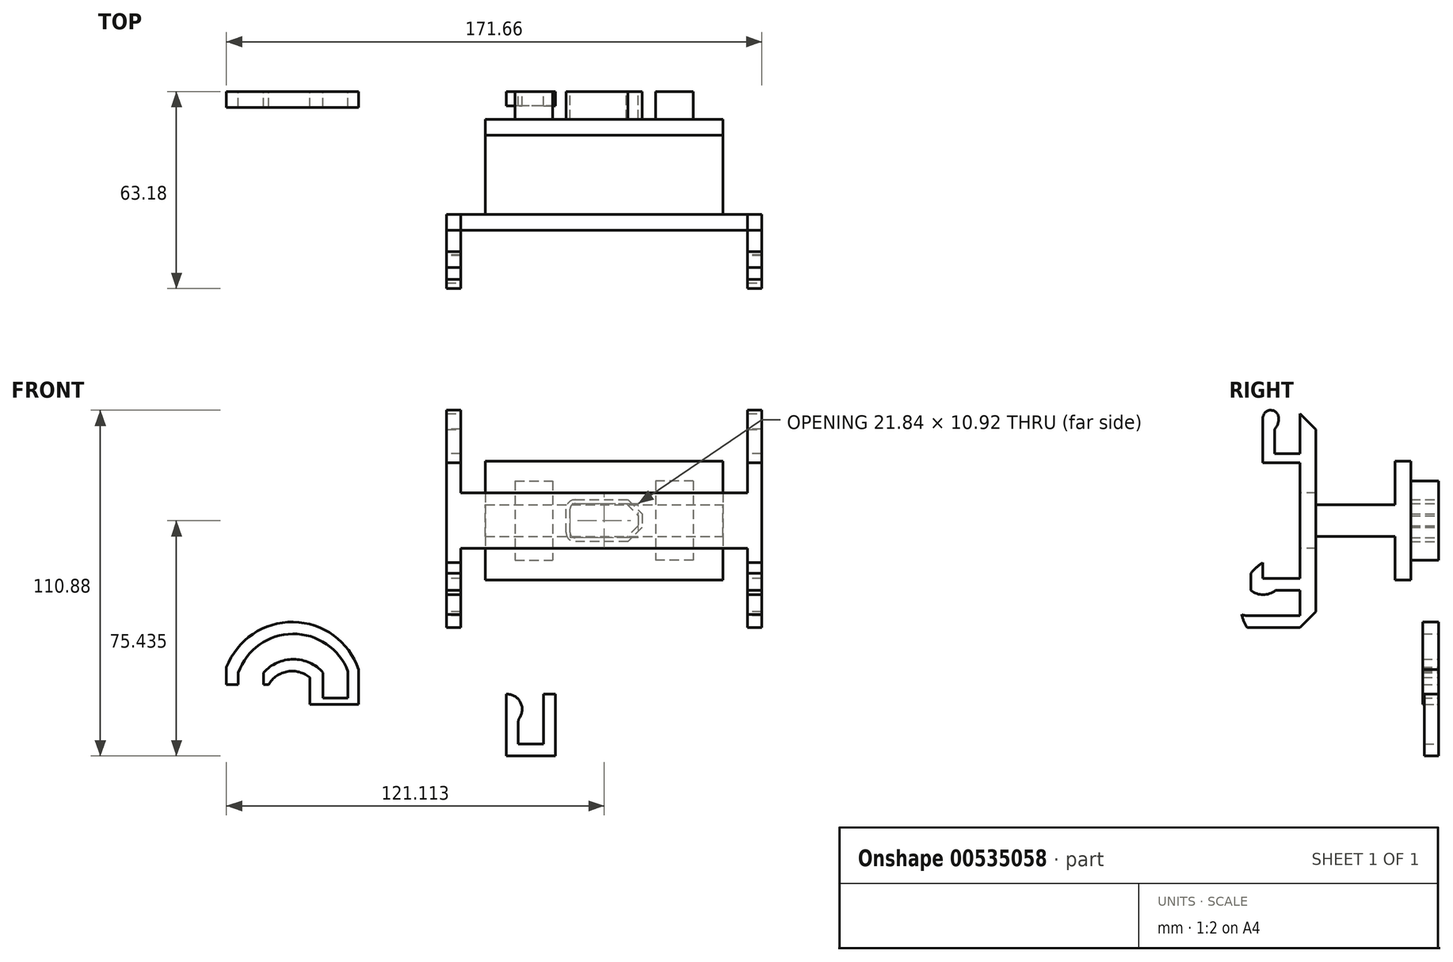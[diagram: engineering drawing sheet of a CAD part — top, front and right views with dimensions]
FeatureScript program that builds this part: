
annotation { "Feature Type Name" : "Feature", "Feature Type Description" : "" }
export const myFeature = defineFeature(function(context is Context, id is Id, definition is map)
    precondition{}
    {
        {
            var Q0;
            Q0=qCreatedBy(makeId("Front.planeOp"),FACE);
            var sketch = newSketch(context, id + "F0", { "sketchPlane" : qUnion([Q0])});
            skArc(sketch, "E0", {"start": v(-13.67, 11.5) * mm, "mid": v(-23.2, 15.8) * mm, "end": v(-32.72, 11.5) * mm});
            skArc(sketch, "E1", {"start": v(-5.68, 11.86) * mm, "mid": v(-23.39, 23.92) * mm, "end": v(-40.85, 11.5) * mm});
            skLineSegment(sketch, "E2", {"start": v(-13.67, 11.5) * mm, "end": v(-13.67, 3.37) * mm});
            skLineSegment(sketch, "E3", {"start": v(-13.67, 3.37) * mm, "end": v(-5.68, 3.37) * mm});
            skLineSegment(sketch, "E4", {"start": v(-5.68, 3.37) * mm, "end": v(-5.68, 11.86) * mm});
            skArc(sketch, "E5.0", {"start": v(-17.86, 9.9) * mm, "mid": v(-25.04, 11.87) * mm, "end": v(-31.2, 7.69) * mm});
            skArc(sketch, "E5.1", {"start": v(-2.25, 12.53) * mm, "mid": v(-23.21, 27.73) * mm, "end": v(-44.66, 13.21) * mm});
            skLineSegment(sketch, "E5.2", {"start": v(-2.25, 1.34) * mm, "end": v(-2.25, 12.53) * mm});
            skLineSegment(sketch, "E5.3", {"start": v(-31.2, 7.69) * mm, "end": v(-32.72, 7.69) * mm});
            skLineSegment(sketch, "E5.4", {"start": v(-17.86, 1.34) * mm, "end": v(-2.25, 1.34) * mm});
            skLineSegment(sketch, "E5.5", {"start": v(-17.86, 9.9) * mm, "end": v(-17.86, 1.34) * mm});
            skLineSegment(sketch, "E6", {"start": v(-32.72, 11.5) * mm, "end": v(-32.72, 7.69) * mm});
            skLineSegment(sketch, "E7", {"start": v(-40.85, 11.5) * mm, "end": v(-40.85, 7.69) * mm});
            skLineSegment(sketch, "E8.trimOffspring", {"start": v(-40.85, 7.69) * mm, "end": v(-44.66, 7.69) * mm});
            skLineSegment(sketch, "E9", {"start": v(-44.66, 7.69) * mm, "end": v(-44.66, 13.21) * mm});
            skSolve(sketch);
        }
        {
            var Q0;
            Q0 = qSketchRegion(id + "F0", true);
            extrude(context, id + "F1", {"entities" : qUnion([Q0]), "depth" : 5.08 * mm, "offsetDistance" : 25.4 * mm});
        }
        {
            var Q0;
            Q0=qCreatedBy(makeId("Front.planeOp"),FACE);
            var sketch = newSketch(context, id + "F2", { "sketchPlane" : qUnion([Q0])});
            skLineSegment(sketch, "E10", {"start": v(60.82, 4.57) * mm, "end": v(60.82, -11.43) * mm});
            skLineSegment(sketch, "E11", {"start": v(60.82, -11.43) * mm, "end": v(57.01, -11.43) * mm});
            skLineSegment(sketch, "E12", {"start": v(57.01, -11.43) * mm, "end": v(48.88, -11.43) * mm});
            skLineSegment(sketch, "E13", {"start": v(48.88, -11.43) * mm, "end": v(48.88, -3.56) * mm});
            skLineSegment(sketch, "E14", {"start": v(48.88, -11.43) * mm, "end": v(45.07, -11.43) * mm});
            skLineSegment(sketch, "E15", {"start": v(57.01, -11.43) * mm, "end": v(57.01, 4.57) * mm});
            skLineSegment(sketch, "E16", {"start": v(48.88, -11.43) * mm, "end": v(48.88, -15.24) * mm});
            skLineSegment(sketch, "E17", {"start": v(60.82, -11.43) * mm, "end": v(60.82, -15.24) * mm});
            skLineSegment(sketch, "E18", {"start": v(60.82, -15.24) * mm, "end": v(45.07, -15.24) * mm});
            skPoint(sketch, "E19.endSnap0", {"position": v(45.58, 10.16) * mm});
            skLineSegment(sketch, "E20", {"start": v(48.88, 0) * mm, "end": v(50.15, 0) * mm});
            skLineSegment(sketch, "E21", {"start": v(45.07, -15.24) * mm, "end": v(45.07, 4.57) * mm});
            skLineSegment(sketch, "E22", {"start": v(57.01, 4.57) * mm, "end": v(60.82, 4.57) * mm});
            skArc(sketch, "E23", {"start": v(48.88, -3.56) * mm, "mid": v(49.7, 1.78) * mm, "end": v(45.07, 4.57) * mm});
            skSolve(sketch);
        }
        {
            var Q0;
            Q0=makeQuery(id+"F2.imprint","IMPRINT",FACE,{"disambiguationData":[TD([[makeQuery(id+"F2.imprint","IMPRINT",EDGE,{"derivedFrom":sQuery(id+"F2.wireOp",EDGE,"RD1xtZW0-n7MP-K1y6-x4sb-vJHUDeZWFKJs")}),1.0]])]});
            var Q1;
            {var subQ0=sQuery(id+"F2.wireOp",EDGE,"E14");Q1=makeQuery(id+"F2.imprint","IMPRINT",FACE,{"disambiguationData":[TD([[makeQuery(id+"F2.imprint","IMPRINT",EDGE,{"derivedFrom":subQ0}),1.0]])]});}
            var Q2;
            {var subQ3=sQuery(id+"F2.wireOp",EDGE,"tBU92qzq-POFk-Bsx7-1rhX-yegVpMIyp9l8");Q2=makeQuery(id+"F2.imprint","IMPRINT",FACE,{"disambiguationData":[TD([[makeQuery(id+"F2.imprint","IMPRINT",EDGE,{"derivedFrom":subQ3}),1.0]])]});}
            var Q3;
            Q3=makeQuery(id+"F2.imprint","IMPRINT",FACE,{"disambiguationData":[TD([[makeQuery(id+"F2.imprint","IMPRINT",EDGE,{"derivedFrom":sQuery(id+"F2.wireOp",EDGE,"E11")}),1.0]])]});
            var Q4;
            Q4=makeQuery(id+"F2.imprint","IMPRINT",FACE,{"disambiguationData":[TD([[makeQuery(id+"F2.imprint","IMPRINT",EDGE,{"derivedFrom":sQuery(id+"F2.wireOp",EDGE,"E13")}),1.0]])]});
            var Q5;
            {var subQ4=sQuery(id+"F2.wireOp",EDGE,"hMDouHN4-NCv2-R56o-Xmj0-efINNTKzQc0g");Q5=makeQuery(id+"F2.imprint","IMPRINT",FACE,{"disambiguationData":[TD([[makeQuery(id+"F2.imprint","IMPRINT",EDGE,{"derivedFrom":subQ4}),1.0]])]});}
            var Q6;
            {var subQ0=sQuery(id+"F2.wireOp",EDGE,"O27wem4o-anWz-oDyt-zTwi-oJhownXQFu4R");Q6=makeQuery(id+"F2.imprint","IMPRINT",FACE,{"disambiguationData":[TD([[makeQuery(id+"F2.imprint","IMPRINT",EDGE,{"derivedFrom":subQ0}),1.0]])]});}
            var Q7;
            {var subQ2=sQuery(id+"F2.wireOp",EDGE,"pY1vVk8C-6wPH-gzvO-LD2K-0AUz0O4XDGy1");var subQ6=makeQuery(id+"F2.imprint","IMPRINT",VERTEX,{"disambiguationData":[OD(0.0)],"derivedFrom":subQ2});Q7=makeQuery(id+"F2.imprint","IMPRINT",FACE,{"disambiguationData":[TD([[makeQuery(id+"F2.imprint","IMPRINT",EDGE,{"disambiguationData":[TD([[subQ6,-1.0]])],"derivedFrom":subQ2}),1.0]])]});}
            var Q8;
            {var subQ2=sQuery(id+"F2.wireOp",EDGE,"pY1vVk8C-6wPH-gzvO-LD2K-0AUz0O4XDGy1");var subQ7=makeQuery(id+"F2.imprint","IMPRINT",VERTEX,{"disambiguationData":[OD(0.0)],"derivedFrom":subQ2});Q8=makeQuery(id+"F2.imprint","IMPRINT",FACE,{"disambiguationData":[TD([[makeQuery(id+"F2.imprint","IMPRINT",EDGE,{"disambiguationData":[TD([[subQ7,-1.0]])],"derivedFrom":subQ2}),-1.0]])]});}
            var Q9;
            Q9=makeQuery(id+"F2.imprint","IMPRINT",FACE,{"disambiguationData":[TD([[makeQuery(id+"F2.imprint","IMPRINT",EDGE,{"derivedFrom":sQuery(id+"F2.wireOp",EDGE,"E10")}),-1.0]])]});
            var Q10;
            {var subQ2=sQuery(id+"F2.wireOp",EDGE,"E14");Q10=makeQuery(id+"F2.imprint","IMPRINT",FACE,{"disambiguationData":[TD([[makeQuery(id+"F2.imprint","IMPRINT",EDGE,{"derivedFrom":subQ2}),-1.0]])]});}
            extrude(context, id + "F3", {"entities" : qUnion([Q0, Q1, Q2, Q3, Q4, Q5, Q6, Q7, Q8, Q9, Q10]), "depth" : 4.57 * mm, "offsetDistance" : 25.4 * mm});
        }
        {
            var Q0;
            Q0=makeQuery(id+"F3.opExtrude","SWEPT_EDGE",EDGE,{"disambiguationData":[OSD([sQuery(id+"F2.wireOp",EDGE,"E13"),sQuery(id+"F2.wireOp",EDGE,"E23")])]});
            fillet(context, id + "F4", {"entities" : qUnion([Q0]), "radius" : 2.54 * mm, "tangentPropagation" : true, "allowEdgeOverflow" : false});
        }
        {
            var Q0;
            Q0=qCreatedBy(makeId("Front.planeOp"),FACE);
            var sketch = newSketch(context, id + "F5", { "sketchPlane" : qUnion([Q0])});
            skArc(sketch, "E24.0", {"start": v(67.18, 54.73) * mm, "mid": v(66.01, 55.22) * mm, "end": v(65.53, 56.39) * mm});
            skLineSegment(sketch, "E24.1", {"start": v(83.55, 54.73) * mm, "end": v(67.18, 54.73) * mm});
            skLineSegment(sketch, "E24.2", {"start": v(65.53, 56.39) * mm, "end": v(65.53, 64) * mm});
            skLineSegment(sketch, "E24.3", {"start": v(87.38, 58.56) * mm, "end": v(83.55, 54.73) * mm});
            skArc(sketch, "E24.4", {"start": v(65.53, 64) * mm, "mid": v(66.01, 65.17) * mm, "end": v(67.18, 65.66) * mm});
            skLineSegment(sketch, "E24.5", {"start": v(67.18, 65.66) * mm, "end": v(83.55, 65.66) * mm});
            skLineSegment(sketch, "E24.6", {"start": v(83.55, 65.66) * mm, "end": v(87.38, 61.83) * mm});
            skLineSegment(sketch, "E24.7", {"start": v(87.38, 61.83) * mm, "end": v(87.38, 58.56) * mm});
            skLineSegment(sketch, "E25.0", {"start": v(64.26, 56.39) * mm, "end": v(64.26, 64) * mm});
            skArc(sketch, "E25.1", {"start": v(67.18, 53.46) * mm, "mid": v(65.12, 54.32) * mm, "end": v(64.26, 56.39) * mm});
            skArc(sketch, "E25.2", {"start": v(64.26, 64) * mm, "mid": v(65.12, 66.07) * mm, "end": v(67.18, 66.93) * mm});
            skLineSegment(sketch, "E25.3", {"start": v(84.07, 53.46) * mm, "end": v(67.18, 53.46) * mm});
            skLineSegment(sketch, "E25.4", {"start": v(67.18, 66.93) * mm, "end": v(84.07, 66.93) * mm});
            skLineSegment(sketch, "E25.5", {"start": v(84.07, 66.93) * mm, "end": v(88.65, 62.36) * mm});
            skLineSegment(sketch, "E25.6", {"start": v(88.65, 62.36) * mm, "end": v(88.65, 58.03) * mm});
            skLineSegment(sketch, "E25.7", {"start": v(88.65, 58.03) * mm, "end": v(84.07, 53.46) * mm});
            skPoint(sketch, "E26.0", {"position": v(38.33, 41.15) * mm});
            skLineSegment(sketch, "E27.bottom", {"start": v(47.88, 72.9) * mm, "end": v(59.94, 72.9) * mm});
            skLineSegment(sketch, "E27.top", {"start": v(47.88, 47.5) * mm, "end": v(59.94, 47.5) * mm});
            skLineSegment(sketch, "E27.left", {"start": v(47.88, 72.9) * mm, "end": v(47.88, 47.5) * mm});
            skLineSegment(sketch, "E27.right", {"start": v(59.94, 72.9) * mm, "end": v(59.94, 47.5) * mm});
            skLineSegment(sketch, "E28.MirrorCS", {"start": v(92.96, 72.9) * mm, "end": v(92.96, 47.5) * mm});
            skLineSegment(sketch, "E29.MirrorCS", {"start": v(105.03, 72.9) * mm, "end": v(92.96, 72.9) * mm});
            skLineSegment(sketch, "E30.MirrorCS", {"start": v(105.03, 72.9) * mm, "end": v(105.03, 47.5) * mm});
            skLineSegment(sketch, "E31.MirrorCS", {"start": v(105.03, 47.5) * mm, "end": v(92.96, 47.5) * mm});
            skSolve(sketch);
        }
        {
            var Q0;
            Q0 = qSketchRegion(id + "F5", true);
            extrude(context, id + "F6", {"entities" : qUnion([Q0]), "depth" : 8.9 * mm, "offsetDistance" : 25.4 * mm});
        }
        {
            var Q0;
            Q0=makeQuery(id+"F6.opExtrude","CAP_FACE",FACE,{"disambiguationData":[OSD([sQuery(id+"F5.wireOp",EDGE,"E27.bottom"),sQuery(id+"F5.wireOp",EDGE,"E27.top"),sQuery(id+"F5.wireOp",EDGE,"E27.left"),sQuery(id+"F5.wireOp",EDGE,"E27.right")])],"isStart":false});
            var sketch = newSketch(context, id + "F7", { "sketchPlane" : qUnion([Q0])});
            skPoint(sketch, "E32.0", {"position": v(105.03, 72.9) * mm});
            skLineSegment(sketch, "E33", {"start": v(47.88, 47.5) * mm, "end": v(105.03, 72.9) * mm});
            skPoint(sketch, "E34.0", {"position": v(105.03, 47.5) * mm});
            skLineSegment(sketch, "E35", {"start": v(47.88, 72.9) * mm, "end": v(105.03, 47.5) * mm});
            skLineSegment(sketch, "E36.bottom", {"start": v(114.58, 79.25) * mm, "end": v(38.33, 79.25) * mm});
            skLineSegment(sketch, "E36.top", {"start": v(114.58, 41.15) * mm, "end": v(38.33, 41.15) * mm});
            skLineSegment(sketch, "E36.left", {"start": v(114.58, 79.25) * mm, "end": v(114.58, 41.15) * mm});
            skLineSegment(sketch, "E36.right", {"start": v(38.33, 79.25) * mm, "end": v(38.33, 41.15) * mm});
            skPoint(sketch, "E36.middle", {"position": v(76.45, 60.2) * mm});
            skSolve(sketch);
        }
        {
            var Q0;
            Q0=makeQuery(id+"F7.imprint","IMPRINT",FACE,{"disambiguationData":[TD([[makeQuery(id+"F7.imprint","IMPRINT",EDGE,{"derivedFrom":sQuery(id+"F7.wireOp",EDGE,"E36.bottom")}),1.0]])]});
            var Q1;
            {var subQ1=makeQuery(id+"F6.opExtrude","CAP_EDGE",EDGE,{"disambiguationData":[OSD([sQuery(id+"F5.wireOp",EDGE,"E27.bottom")])],"isStart":false});Q1=makeQuery(id+"F7.imprint","IMPRINT",FACE,{"disambiguationData":[TD([[makeQuery(id+"F7.imprint","IMPRINT",EDGE,{"derivedFrom":subQ1}),-1.0]])]});}
            var Q2;
            {var subQ0=sQuery(id+"F7.wireOp",EDGE,"E35");var subQ1=sQuery(id+"F7.wireOp",EDGE,"E33");var subQ2=makeQuery(id+"F7.imprint","INTERSECT",VERTEX,{"derivedFrom":[subQ1,subQ0]});Q2=makeQuery(id+"F7.imprint","IMPRINT",FACE,{"disambiguationData":[TD([[makeQuery(id+"F7.imprint","IMPRINT",EDGE,{"disambiguationData":[TD([[subQ2,1.0]])],"derivedFrom":subQ1}),1.0]])]});}
            var Q3;
            {var subQ1=makeQuery(id+"F6.opExtrude","CAP_EDGE",EDGE,{"disambiguationData":[OSD([sQuery(id+"F5.wireOp",EDGE,"E27.left")])],"isStart":false});Q3=makeQuery(id+"F7.imprint","IMPRINT",FACE,{"disambiguationData":[TD([[makeQuery(id+"F7.imprint","IMPRINT",EDGE,{"derivedFrom":subQ1}),1.0]])]});}
            var Q4;
            {var subQ1=makeQuery(id+"F6.opExtrude","CAP_EDGE",EDGE,{"disambiguationData":[OSD([sQuery(id+"F5.wireOp",EDGE,"E27.top")])],"isStart":false});Q4=makeQuery(id+"F7.imprint","IMPRINT",FACE,{"disambiguationData":[TD([[makeQuery(id+"F7.imprint","IMPRINT",EDGE,{"derivedFrom":subQ1}),1.0]])]});}
            extrude(context, id + "F8", {"entities" : qUnion([Q0, Q1, Q2, Q3, Q4]), "depth" : 5.08 * mm, "offsetDistance" : 25.4 * mm});
        }
        {
            var Q0;
            Q0=makeQuery(id+"F8.opExtrude","SWEPT_FACE",FACE,{"disambiguationData":[OSD([sQuery(id+"F7.wireOp",EDGE,"E36.right")])]});
            cPlane(context, id + "F9", {"entities" : qUnion([Q0]), "cplaneType" : CPlaneType.OFFSET, "offset" : 38.13 * mm, "oppositeDirection" : true, "width" : 152.4 * mm, "height" : 152.4 * mm});
        }
        {
            var Q0;
            Q0=qCreatedBy(id+"F9.planeOp",FACE);
            var sketch = newSketch(context, id + "F10", { "sketchPlane" : qUnion([Q0])});
            skLineSegment(sketch, "E37.0", {"start": v(13.97, 79.25) * mm, "end": v(13.97, 41.15) * mm});
            skLineSegment(sketch, "E38", {"start": v(13.97, 60.2) * mm, "end": v(13.97, 65.28) * mm});
            skLineSegment(sketch, "E39", {"start": v(13.97, 60.2) * mm, "end": v(13.97, 94.49) * mm});
            skLineSegment(sketch, "E40", {"start": v(13.97, 65.28) * mm, "end": v(39.37, 65.28) * mm});
            skLineSegment(sketch, "E41", {"start": v(39.37, 65.28) * mm, "end": v(39.37, 94.49) * mm});
            skLineSegment(sketch, "E42", {"start": v(13.97, 60.2) * mm, "end": v(44.45, 60.2) * mm});
            skLineSegment(sketch, "E43", {"start": v(44.45, 60.2) * mm, "end": v(44.45, 94.49) * mm});
            skLineSegment(sketch, "E44", {"start": v(44.45, 94.49) * mm, "end": v(39.37, 94.49) * mm});
            skLineSegment(sketch, "E45.MirrorCS", {"start": v(13.97, 55.12) * mm, "end": v(39.37, 55.12) * mm});
            skLineSegment(sketch, "E46.MirrorCS", {"start": v(44.45, 60.2) * mm, "end": v(44.45, 25.9) * mm});
            skLineSegment(sketch, "E47.MirrorCS", {"start": v(39.37, 55.12) * mm, "end": v(39.37, 25.9) * mm});
            skLineSegment(sketch, "E48.MirrorCS", {"start": v(44.45, 25.9) * mm, "end": v(39.37, 25.9) * mm});
            skSolve(sketch);
        }
        {
            var Q0;
            {var subQ1=sQuery(id+"F10.wireOp",EDGE,"E40");Q0=makeQuery(id+"F10.imprint","IMPRINT",FACE,{"disambiguationData":[TD([[makeQuery(id+"F10.imprint","IMPRINT",EDGE,{"derivedFrom":subQ1}),-1.0]])]});}
            var Q1;
            {var subQ1=sQuery(id+"F10.wireOp",EDGE,"E42");Q1=makeQuery(id+"F10.imprint","IMPRINT",FACE,{"disambiguationData":[TD([[makeQuery(id+"F10.imprint","IMPRINT",EDGE,{"derivedFrom":subQ1}),-1.0]])]});}
            extrude(context, id + "F11", {"entities" : qUnion([Q0, Q1]), "operationType" : NewBodyOperationType.ADD, "depth" : 101.1 * mm, "offsetDistance" : 25.4 * mm, "symmetric" : true});
        }
        {
            var Q0;
            Q0=makeQuery(id+"F11.opExtrude","SWEPT_FACE",FACE,{"disambiguationData":[OSD([sQuery(id+"F10.wireOp",EDGE,"E40")])]});
            var sketch = newSketch(context, id + "F12", { "sketchPlane" : qUnion([Q0])});
            skLineSegment(sketch, "E49.0", {"start": v(25.9, -13.97) * mm, "end": v(25.9, -39.37) * mm});
            skLineSegment(sketch, "E50.0", {"start": v(127, -13.97) * mm, "end": v(127, -39.37) * mm});
            skLineSegment(sketch, "E51", {"start": v(25.9, -13.97) * mm, "end": v(38.33, -13.97) * mm});
            skLineSegment(sketch, "E52", {"start": v(38.33, -13.97) * mm, "end": v(38.33, -39.37) * mm});
            skLineSegment(sketch, "E53", {"start": v(38.33, -39.37) * mm, "end": v(25.9, -39.37) * mm});
            skLineSegment(sketch, "E54", {"start": v(127, -13.97) * mm, "end": v(114.58, -13.97) * mm});
            skLineSegment(sketch, "E55", {"start": v(114.58, -13.97) * mm, "end": v(114.58, -39.37) * mm});
            skLineSegment(sketch, "E56", {"start": v(114.58, -39.37) * mm, "end": v(127, -39.37) * mm});
            skSolve(sketch);
        }
        {
            var Q0;
            Q0 = qSketchRegion(id + "F12", true);
            extrude(context, id + "F13", {"entities" : qUnion([Q0]), "operationType" : NewBodyOperationType.REMOVE, "oppositeDirection" : true, "depth" : 25.4 * mm, "offsetDistance" : 25.4 * mm});
        }
        {
            var Q0;
            Q0=makeQuery(id+"F11.opExtrude","SWEPT_FACE",FACE,{"disambiguationData":[OSD([sQuery(id+"F10.wireOp",EDGE,"E43"),sQuery(id+"F10.wireOp",EDGE,"E46.MirrorCS")])]});
            var sketch = newSketch(context, id + "F14", { "sketchPlane" : qUnion([Q0])});
            skLineSegment(sketch, "E57.0", {"start": v(25.9, 25.9) * mm, "end": v(25.9, 94.49) * mm});
            skLineSegment(sketch, "E58.0", {"start": v(127, 25.9) * mm, "end": v(127, 94.49) * mm});
            skLineSegment(sketch, "E59", {"start": v(25.9, 94.49) * mm, "end": v(30.48, 94.49) * mm});
            skLineSegment(sketch, "E60", {"start": v(30.48, 94.49) * mm, "end": v(30.48, 69.09) * mm});
            skLineSegment(sketch, "E61", {"start": v(30.48, 69.09) * mm, "end": v(122.43, 69.09) * mm});
            skLineSegment(sketch, "E62", {"start": v(122.43, 69.09) * mm, "end": v(122.43, 94.49) * mm});
            skLineSegment(sketch, "E63", {"start": v(30.48, 94.49) * mm, "end": v(122.43, 94.49) * mm});
            skLineSegment(sketch, "E64", {"start": v(25.9, 60.2) * mm, "end": v(51.81, 60.2) * mm});
            skPoint(sketch, "E64.endSnap0", {"position": v(25.9, 60.2) * mm});
            skLineSegment(sketch, "E65.MirrorCS", {"start": v(30.48, 51.3) * mm, "end": v(122.43, 51.3) * mm});
            skLineSegment(sketch, "E66.MirrorCS", {"start": v(30.48, 25.9) * mm, "end": v(30.48, 51.3) * mm});
            skLineSegment(sketch, "E67.MirrorCS", {"start": v(30.48, 25.9) * mm, "end": v(122.43, 25.9) * mm});
            skLineSegment(sketch, "E68.MirrorCS", {"start": v(122.43, 51.3) * mm, "end": v(122.43, 25.9) * mm});
            skLineSegment(sketch, "E69", {"start": v(127, 94.49) * mm, "end": v(122.43, 94.49) * mm});
            skSolve(sketch);
        }
        {
            var Q0;
            Q0 = qSketchRegion(id + "F14", true);
            extrude(context, id + "F15", {"entities" : qUnion([Q0]), "operationType" : NewBodyOperationType.REMOVE, "oppositeDirection" : true, "depth" : 25.4 * mm, "offsetDistance" : 25.4 * mm});
        }
        {
            var Q0;
            Q0=qCreatedBy(id+"F9.planeOp",FACE);
            var sketch = newSketch(context, id + "F16", { "sketchPlane" : qUnion([Q0])});
            skLineSegment(sketch, "E70", {"start": v(44.45, 81.76) * mm, "end": v(44.45, 77.95) * mm});
            skLineSegment(sketch, "E71.MirrorCS", {"start": v(52.58, 93.19) * mm, "end": v(51.3, 93.19) * mm});
            skLineSegment(sketch, "E72.MirrorCS", {"start": v(52.58, 81.76) * mm, "end": v(52.58, 89.63) * mm});
            skLineSegment(sketch, "E73.MirrorCS", {"start": v(56.39, 77.95) * mm, "end": v(56.39, 97.76) * mm});
            skLineSegment(sketch, "E74.MirrorCS", {"start": v(52.58, 81.76) * mm, "end": v(52.58, 77.95) * mm});
            skLineSegment(sketch, "E75.MirrorCS", {"start": v(52.58, 81.76) * mm, "end": v(56.39, 81.76) * mm});
            skArc(sketch, "E76.MirrorCS", {"start": v(52.58, 89.63) * mm, "mid": v(51.76, 94.97) * mm, "end": v(56.39, 97.76) * mm});
            skLineSegment(sketch, "E77.MirrorCS", {"start": v(44.45, 81.76) * mm, "end": v(52.58, 81.76) * mm});
            skLineSegment(sketch, "E78.MirrorCS", {"start": v(44.45, 78.74) * mm, "end": v(56.39, 78.74) * mm});
            skPoint(sketch, "E79.0", {"position": v(44.45, 98.3) * mm});
            skLineSegment(sketch, "E80", {"start": v(44.45, 60.2) * mm, "end": v(66.7, 60.2) * mm});
            skLineSegment(sketch, "E81.MirrorCS", {"start": v(44.45, 41.65) * mm, "end": v(56.39, 41.65) * mm});
            skLineSegment(sketch, "E82", {"start": v(56.39, 41.65) * mm, "end": v(56.39, 49.27) * mm});
            skLineSegment(sketch, "E83", {"start": v(56.39, 49.27) * mm, "end": v(60.2, 49.27) * mm});
            skLineSegment(sketch, "E84", {"start": v(60.2, 49.27) * mm, "end": v(60.2, 37.84) * mm});
            skLineSegment(sketch, "E85", {"start": v(44.45, 29.72) * mm, "end": v(68.33, 29.72) * mm});
            skLineSegment(sketch, "E86.0", {"start": v(44.45, 25.9) * mm, "end": v(44.45, 94.49) * mm});
            skLineSegment(sketch, "E87", {"start": v(52.32, 37.84) * mm, "end": v(44.45, 37.84) * mm});
            skLineSegment(sketch, "E88", {"start": v(44.45, 37.84) * mm, "end": v(52.32, 37.84) * mm});
            skArc(sketch, "E89", {"start": v(52.32, 37.84) * mm, "mid": v(56.26, 36.48) * mm, "end": v(60.2, 37.84) * mm});
            skLineSegment(sketch, "E90", {"start": v(44.45, 29.72) * mm, "end": v(44.45, 25.9) * mm});
            skLineSegment(sketch, "E91", {"start": v(44.45, 25.9) * mm, "end": v(72.14, 25.9) * mm});
            skLineSegment(sketch, "E92", {"start": v(68.33, 29.72) * mm, "end": v(68.33, 49.27) * mm});
            skLineSegment(sketch, "E93", {"start": v(68.33, 49.27) * mm, "end": v(72.14, 49.27) * mm});
            skLineSegment(sketch, "E94", {"start": v(72.14, 49.27) * mm, "end": v(72.14, 25.9) * mm});
            skSolve(sketch);
        }
        {
            var Q0;
            Q0 = qSketchRegion(id + "F16", true);
            var Q1;
            Q1=makeQuery(id+"F15.boolean.opBoolean","COPY",FACE,{"derivedFrom":makeQuery(id+"F15.opExtrude","SWEPT_FACE",FACE,{"disambiguationData":[OSD([sQuery(id+"F14.wireOp",EDGE,"E60")])]})});
            extrude(context, id + "F17", {"entities" : qUnion([Q0]), "operationType" : NewBodyOperationType.ADD, "oppositeDirection" : true, "depth" : 101.1 * mm, "endBoundEntityFace" : qUnion([Q1]), "offsetDistance" : 25.4 * mm, "symmetric" : true});
        }
        {
            var Q0;
            Q0=makeQuery(id+"F17.opExtrude","SWEPT_EDGE",EDGE,{"disambiguationData":[OSD([sQuery(id+"F16.wireOp",EDGE,"E73.MirrorCS"),sQuery(id+"F16.wireOp",EDGE,"E76.MirrorCS")])]});
            fillet(context, id + "F18", {"entities" : qUnion([Q0]), "radius" : 2.54 * mm, "tangentPropagation" : true, "allowEdgeOverflow" : false});
        }
        {
            var Q0;
            {var subQ1=sQuery(id+"F10.wireOp",EDGE,"E44");var subQ2=sQuery(id+"F10.wireOp",EDGE,"E41");Q0=makeQuery(id+"F15.boolean.opBoolean","SPLIT",EDGE,{"disambiguationData":[TD([makeQuery(id+"F15.opExtrude","SWEPT_FACE",FACE,{"disambiguationData":[OSD([sQuery(id+"F14.wireOp",EDGE,"E60")])]})])],"derivedFrom":makeQuery(id+"F11.opExtrude","SWEPT_EDGE",EDGE,{"disambiguationData":[OSD([subQ2,subQ1])]})});}
            chamfer(context, id + "F19", {"entities" : qUnion([Q0]), "width" : 5.08 * mm, "tangentPropagation" : true});
        }
        {
            var Q0;
            {var subQ1=sQuery(id+"F10.wireOp",EDGE,"E41");var subQ2=sQuery(id+"F10.wireOp",EDGE,"E44");Q0=makeQuery(id+"F15.boolean.opBoolean","SPLIT",EDGE,{"disambiguationData":[TD([makeQuery(id+"F15.opExtrude","SWEPT_FACE",FACE,{"disambiguationData":[OSD([sQuery(id+"F14.wireOp",EDGE,"E62")])]})])],"derivedFrom":makeQuery(id+"F11.opExtrude","SWEPT_EDGE",EDGE,{"disambiguationData":[OSD([subQ1,subQ2])]})});}
            chamfer(context, id + "F20", {"entities" : qUnion([Q0]), "width" : 5.08 * mm, "tangentPropagation" : true});
        }
        {
            var Q0;
            Q0=makeQuery(id+"F17.opExtrude","SWEPT_FACE",FACE,{"disambiguationData":[OSD([sQuery(id+"F16.wireOp",EDGE,"E78.MirrorCS")])]});
            var sketch = newSketch(context, id + "F21", { "sketchPlane" : qUnion([Q0])});
            skPoint(sketch, "E95.0", {"position": v(30.48, 44.45) * mm});
            skPoint(sketch, "E96.0", {"position": v(122.43, 44.45) * mm});
            skLineSegment(sketch, "E97", {"start": v(30.48, 44.45) * mm, "end": v(30.48, 56.39) * mm});
            skLineSegment(sketch, "E98", {"start": v(122.43, 44.45) * mm, "end": v(30.48, 44.45) * mm});
            skLineSegment(sketch, "E99.0", {"start": v(127, 72.14) * mm, "end": v(25.9, 72.14) * mm});
            skLineSegment(sketch, "E100", {"start": v(122.43, 44.45) * mm, "end": v(122.43, 72.14) * mm});
            skLineSegment(sketch, "E101", {"start": v(122.43, 72.14) * mm, "end": v(30.48, 72.14) * mm});
            skLineSegment(sketch, "E102", {"start": v(30.48, 72.14) * mm, "end": v(30.48, 56.39) * mm});
            skLineSegment(sketch, "E103", {"start": v(30.48, 44.45) * mm, "end": v(122.43, 44.45) * mm});
            skSolve(sketch);
        }
        {
            var Q0;
            Q0 = qSketchRegion(id + "F21", true);
            extrude(context, id + "F22", {"entities" : qUnion([Q0]), "operationType" : NewBodyOperationType.REMOVE, "oppositeDirection" : true, "depth" : 25.4 * mm, "offsetDistance" : 25.4 * mm});
        }
        {
            var Q0;
            {var subQ0=sQuery(id+"F10.wireOp",EDGE,"E47.MirrorCS");var subQ1=sQuery(id+"F10.wireOp",EDGE,"E48.MirrorCS");Q0=makeQuery(id+"F15.boolean.opBoolean","SPLIT",EDGE,{"disambiguationData":[TD([makeQuery(id+"F15.opExtrude","SWEPT_FACE",FACE,{"disambiguationData":[OSD([sQuery(id+"F14.wireOp",EDGE,"E66.MirrorCS")])]})])],"derivedFrom":makeQuery(id+"F11.opExtrude","SWEPT_EDGE",EDGE,{"disambiguationData":[OSD([subQ0,subQ1])]})});}
            chamfer(context, id + "F23", {"entities" : qUnion([Q0]), "width" : 5.08 * mm, "tangentPropagation" : true});
        }
        {
            var Q0;
            {var subQ0=sQuery(id+"F10.wireOp",EDGE,"E47.MirrorCS");var subQ1=sQuery(id+"F10.wireOp",EDGE,"E48.MirrorCS");Q0=makeQuery(id+"F15.boolean.opBoolean","SPLIT",EDGE,{"disambiguationData":[TD([makeQuery(id+"F15.opExtrude","SWEPT_FACE",FACE,{"disambiguationData":[OSD([sQuery(id+"F14.wireOp",EDGE,"E68.MirrorCS")])]})])],"derivedFrom":makeQuery(id+"F11.opExtrude","SWEPT_EDGE",EDGE,{"disambiguationData":[OSD([subQ0,subQ1])]})});}
            chamfer(context, id + "F24", {"entities" : qUnion([Q0]), "width" : 5.08 * mm, "tangentPropagation" : true});
        }
        {
            var Q0;
            Q0 = qSketchRegion(id + "F21", true);
            extrude(context, id + "F25", {"entities" : qUnion([Q0]), "operationType" : NewBodyOperationType.REMOVE, "oppositeDirection" : true, "depth" : 114.3 * mm, "offsetDistance" : 25.4 * mm, "symmetric" : true});
        }
        {
            var Q0;
            {var subQ1=sQuery(id+"F16.wireOp",EDGE,"E94");var subQ2=sQuery(id+"F16.wireOp",EDGE,"E91");Q0=makeQuery(id+"F25.boolean.opBoolean","SPLIT",EDGE,{"disambiguationData":[TD([makeQuery(id+"F15.boolean.opBoolean","COPY",FACE,{"derivedFrom":makeQuery(id+"F15.opExtrude","SWEPT_FACE",FACE,{"disambiguationData":[OSD([sQuery(id+"F14.wireOp",EDGE,"E68.MirrorCS")])]})})])],"derivedFrom":makeQuery(id+"F17.opExtrude","SWEPT_EDGE",EDGE,{"disambiguationData":[OSD([subQ2,subQ1])]})});}
            var Q1;
            {var subQ1=sQuery(id+"F16.wireOp",EDGE,"E85");var subQ2=sQuery(id+"F16.wireOp",EDGE,"E92");Q1=makeQuery(id+"F25.boolean.opBoolean","SPLIT",EDGE,{"disambiguationData":[TD([makeQuery(id+"F15.boolean.opBoolean","COPY",FACE,{"derivedFrom":makeQuery(id+"F15.opExtrude","SWEPT_FACE",FACE,{"disambiguationData":[OSD([sQuery(id+"F14.wireOp",EDGE,"E68.MirrorCS")])]})})])],"derivedFrom":makeQuery(id+"F17.opExtrude","SWEPT_EDGE",EDGE,{"disambiguationData":[OSD([subQ1,subQ2])]})});}
            fillet(context, id + "F26", {"entities" : qUnion([Q0, Q1]), "radius" : 7.62 * mm, "tangentPropagation" : true, "allowEdgeOverflow" : false});
        }
        {
            var Q0;
            {var subQ1=sQuery(id+"F16.wireOp",EDGE,"E94");var subQ2=sQuery(id+"F16.wireOp",EDGE,"E91");Q0=makeQuery(id+"F25.boolean.opBoolean","SPLIT",EDGE,{"disambiguationData":[TD([makeQuery(id+"F15.boolean.opBoolean","COPY",FACE,{"derivedFrom":makeQuery(id+"F15.opExtrude","SWEPT_FACE",FACE,{"disambiguationData":[OSD([sQuery(id+"F14.wireOp",EDGE,"E66.MirrorCS")])]})})])],"derivedFrom":makeQuery(id+"F17.opExtrude","SWEPT_EDGE",EDGE,{"disambiguationData":[OSD([subQ2,subQ1])]})});}
            var Q1;
            {var subQ1=sQuery(id+"F16.wireOp",EDGE,"E92");var subQ2=sQuery(id+"F16.wireOp",EDGE,"E85");Q1=makeQuery(id+"F25.boolean.opBoolean","SPLIT",EDGE,{"disambiguationData":[TD([makeQuery(id+"F15.boolean.opBoolean","COPY",FACE,{"derivedFrom":makeQuery(id+"F15.opExtrude","SWEPT_FACE",FACE,{"disambiguationData":[OSD([sQuery(id+"F14.wireOp",EDGE,"E66.MirrorCS")])]})})])],"derivedFrom":makeQuery(id+"F17.opExtrude","SWEPT_EDGE",EDGE,{"disambiguationData":[OSD([subQ2,subQ1])]})});}
            fillet(context, id + "F27", {"entities" : qUnion([Q0, Q1]), "radius" : 7.62 * mm, "tangentPropagation" : true, "allowEdgeOverflow" : false});
        }
        {
            var Q0;
            {var subQ0=sQuery(id+"F16.wireOp",EDGE,"E86.0");Q0=makeQuery(id+"F17.boolean.opBoolean","MERGE",FACE,{"derivedFrom":[makeQuery(id+"F11.opExtrude","CAP_FACE",FACE,{"disambiguationData":[OSD([sQuery(id+"F10.wireOp",EDGE,"E37.0"),sQuery(id+"F10.wireOp",EDGE,"E39"),sQuery(id+"F10.wireOp",EDGE,"E40"),sQuery(id+"F10.wireOp",EDGE,"E41"),sQuery(id+"F10.wireOp",EDGE,"E43"),sQuery(id+"F10.wireOp",EDGE,"E44"),sQuery(id+"F10.wireOp",EDGE,"E45.MirrorCS"),sQuery(id+"F10.wireOp",EDGE,"E46.MirrorCS"),sQuery(id+"F10.wireOp",EDGE,"E47.MirrorCS"),sQuery(id+"F10.wireOp",EDGE,"E48.MirrorCS")])],"isStart":true}),makeQuery(id+"F17.opExtrude","CAP_FACE",FACE,{"disambiguationData":[OSD([sQuery(id+"F16.wireOp",EDGE,"E73.MirrorCS"),sQuery(id+"F16.wireOp",EDGE,"E72.MirrorCS"),sQuery(id+"F16.wireOp",EDGE,"E76.MirrorCS"),sQuery(id+"F16.wireOp",EDGE,"E77.MirrorCS"),sQuery(id+"F16.wireOp",EDGE,"E78.MirrorCS"),subQ0])],"isStart":false}),makeQuery(id+"F17.opExtrude","CAP_FACE",FACE,{"disambiguationData":[OSD([sQuery(id+"F16.wireOp",EDGE,"E81.MirrorCS"),sQuery(id+"F16.wireOp",EDGE,"E82"),sQuery(id+"F16.wireOp",EDGE,"E83"),sQuery(id+"F16.wireOp",EDGE,"E84"),subQ0,sQuery(id+"F16.wireOp",EDGE,"E88"),sQuery(id+"F16.wireOp",EDGE,"E89")])],"isStart":false}),makeQuery(id+"F17.opExtrude","CAP_FACE",FACE,{"disambiguationData":[OSD([sQuery(id+"F16.wireOp",EDGE,"E85"),sQuery(id+"F16.wireOp",EDGE,"E90"),sQuery(id+"F16.wireOp",EDGE,"E91"),sQuery(id+"F16.wireOp",EDGE,"E92"),sQuery(id+"F16.wireOp",EDGE,"E93"),sQuery(id+"F16.wireOp",EDGE,"E94")])],"isStart":false})]});}
            var sketch = newSketch(context, id + "F28", { "sketchPlane" : qUnion([Q0])});
            skArc(sketch, "E104", {"start": v(-54.08, 47.92) * mm, "mid": v(-63.06, 37.9) * mm, "end": v(-60.6, 24.66) * mm});
            skPoint(sketch, "E104.centerSnap0", {"position": v(-48.39, 37.84) * mm});
            skPoint(sketch, "E104.centerSnap1", {"position": v(-44.45, 33.78) * mm});
            skArc(sketch, "E105", {"start": v(-60.13, 63.09) * mm, "mid": v(-78.47, 43.35) * mm, "end": v(-74.9, 16.65) * mm});
            skLineSegment(sketch, "E106", {"start": v(-60.13, 63.09) * mm, "end": v(-54.08, 47.92) * mm});
            skLineSegment(sketch, "E107", {"start": v(-60.6, 24.66) * mm, "end": v(-74.9, 16.65) * mm});
            skSolve(sketch);
        }
        {
            var Q0;
            Q0 = qSketchRegion(id + "F28", true);
            var Q1;
            {var subQ0=sQuery(id+"F16.wireOp",EDGE,"E86.0");Q1=makeQuery(id+"F17.boolean.opBoolean","MERGE",FACE,{"derivedFrom":[makeQuery(id+"F11.opExtrude","CAP_FACE",FACE,{"disambiguationData":[OSD([sQuery(id+"F10.wireOp",EDGE,"E37.0"),sQuery(id+"F10.wireOp",EDGE,"E39"),sQuery(id+"F10.wireOp",EDGE,"E40"),sQuery(id+"F10.wireOp",EDGE,"E41"),sQuery(id+"F10.wireOp",EDGE,"E43"),sQuery(id+"F10.wireOp",EDGE,"E44"),sQuery(id+"F10.wireOp",EDGE,"E45.MirrorCS"),sQuery(id+"F10.wireOp",EDGE,"E46.MirrorCS"),sQuery(id+"F10.wireOp",EDGE,"E47.MirrorCS"),sQuery(id+"F10.wireOp",EDGE,"E48.MirrorCS")])],"isStart":false}),makeQuery(id+"F17.opExtrude","CAP_FACE",FACE,{"disambiguationData":[OSD([sQuery(id+"F16.wireOp",EDGE,"E73.MirrorCS"),sQuery(id+"F16.wireOp",EDGE,"E72.MirrorCS"),sQuery(id+"F16.wireOp",EDGE,"E76.MirrorCS"),sQuery(id+"F16.wireOp",EDGE,"E77.MirrorCS"),sQuery(id+"F16.wireOp",EDGE,"E78.MirrorCS"),subQ0])],"isStart":true}),makeQuery(id+"F17.opExtrude","CAP_FACE",FACE,{"disambiguationData":[OSD([sQuery(id+"F16.wireOp",EDGE,"E81.MirrorCS"),sQuery(id+"F16.wireOp",EDGE,"E82"),sQuery(id+"F16.wireOp",EDGE,"E83"),sQuery(id+"F16.wireOp",EDGE,"E84"),subQ0,sQuery(id+"F16.wireOp",EDGE,"E88"),sQuery(id+"F16.wireOp",EDGE,"E89")])],"isStart":true}),makeQuery(id+"F17.opExtrude","CAP_FACE",FACE,{"disambiguationData":[OSD([sQuery(id+"F16.wireOp",EDGE,"E85"),sQuery(id+"F16.wireOp",EDGE,"E90"),sQuery(id+"F16.wireOp",EDGE,"E91"),sQuery(id+"F16.wireOp",EDGE,"E92"),sQuery(id+"F16.wireOp",EDGE,"E93"),sQuery(id+"F16.wireOp",EDGE,"E94")])],"isStart":true})]});}
            extrude(context, id + "F29", {"entities" : qUnion([Q0]), "operationType" : NewBodyOperationType.REMOVE, "endBound" : BoundingType.UP_TO_SURFACE, "oppositeDirection" : true, "depth" : 25.4 * mm, "endBoundEntityFace" : qUnion([Q1]), "offsetDistance" : 25.4 * mm});
        }
    });
